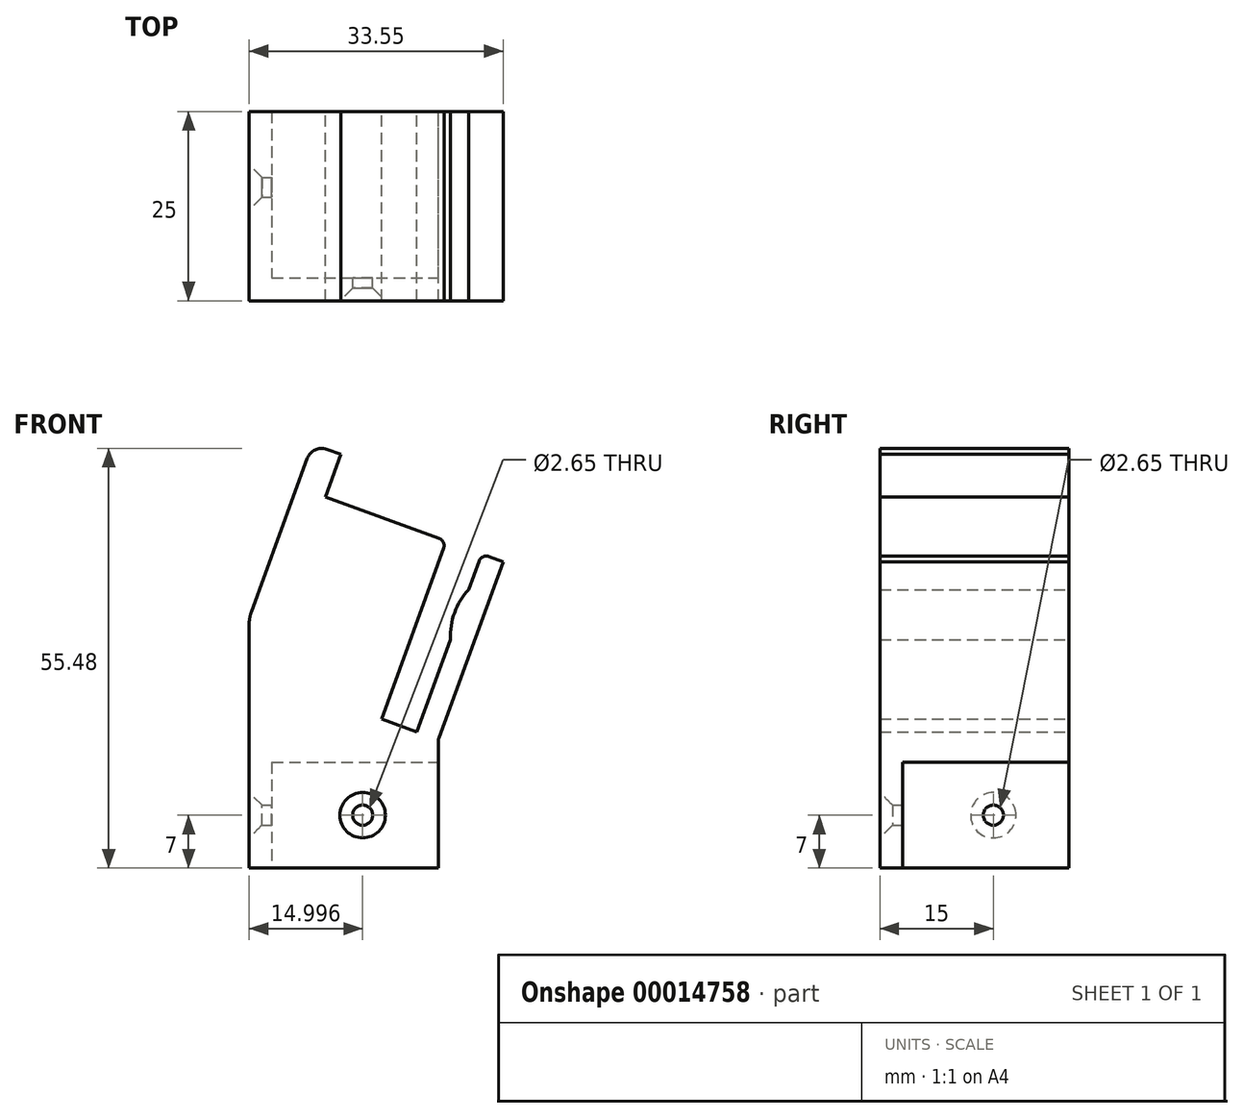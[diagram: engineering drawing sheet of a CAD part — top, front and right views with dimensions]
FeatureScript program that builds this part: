
annotation { "Feature Type Name" : "Feature", "Feature Type Description" : "" }
export const myFeature = defineFeature(function(context is Context, id is Id, definition is map)
    precondition{}
    {
        {
            var Q0;
            Q0=qCreatedBy(makeId("Front.planeOp"),FACE);
            var sketch = newSketch(context, id + "F0", { "sketchPlane" : qUnion([Q0])});
            skLineSegment(sketch, "E0", {"start": v(-18.57, 0) * mm, "end": v(-18.57, 18.15) * mm});
            skLineSegment(sketch, "E1", {"start": v(-8.32, 41.36) * mm, "end": v(-6.46, 40.68) * mm});
            skLineSegment(sketch, "E2", {"start": v(-6.46, 40.68) * mm, "end": v(-8.52, 35.04) * mm});
            skLineSegment(sketch, "E3", {"start": v(-8.52, 35.04) * mm, "end": v(6.52, 29.57) * mm});
            skLineSegment(sketch, "E4", {"start": v(7.12, 28.29) * mm, "end": v(-1.1, 5.74) * mm});
            skLineSegment(sketch, "E5", {"start": v(-1.1, 5.74) * mm, "end": v(3.6, 4.03) * mm});
            skLineSegment(sketch, "E6", {"start": v(3.6, 4.03) * mm, "end": v(8.04, 16.2) * mm});
            skArc(sketch, "E7", {"start": v(10.45, 22.82) * mm, "mid": v(8.56, 19.76) * mm, "end": v(8.04, 16.2) * mm});
            skLineSegment(sketch, "E8", {"start": v(10.45, 22.82) * mm, "end": v(11.82, 26.58) * mm});
            skLineSegment(sketch, "E9", {"start": v(13.1, 27.18) * mm, "end": v(14.98, 26.5) * mm});
            skLineSegment(sketch, "E10", {"start": v(14.98, 26.5) * mm, "end": v(6.49, 3.17) * mm});
            skLineSegment(sketch, "E11", {"start": v(6.43, 2.82) * mm, "end": v(6.43, 0) * mm});
            skLineSegment(sketch, "E12", {"start": v(6.43, 0) * mm, "end": v(-18.57, 0) * mm});
            skLineSegment(sketch, "E13", {"start": v(7.46, 29.23) * mm, "end": v(11.02, 27.93) * mm, "construction": true});
            skLineSegment(sketch, "E14", {"start": v(3.6, 4.03) * mm, "end": v(9.61, 1.84) * mm, "construction": true});
            skLineSegment(sketch, "E15", {"start": v(-10.88, 40.16) * mm, "end": v(-18.27, 19.86) * mm});
            skPoint(sketch, "E15.endSnap0", {"position": v(-18.57, 19.9) * mm});
            skPoint(sketch, "E16.orphan", {"position": v(-18.57, 39.81) * mm});
            skLineSegment(sketch, "E17", {"start": v(-18.57, 0) * mm, "end": v(-18.57, -14) * mm});
            skLineSegment(sketch, "E18", {"start": v(-18.57, -14) * mm, "end": v(6.43, -14) * mm});
            skLineSegment(sketch, "E19", {"start": v(6.43, -14) * mm, "end": v(6.43, 0) * mm});
            skPoint(sketch, "E20.visualSharp", {"position": v(-18.57, 19.04) * mm});
            skArc(sketch, "E20.filletArc", {"start": v(-18.27, 19.86) * mm, "mid": v(-18.5, 19.02) * mm, "end": v(-18.57, 18.15) * mm});
            skPoint(sketch, "E21.visualSharp", {"position": v(-10.2, 42.04) * mm});
            skArc(sketch, "E21.filletArc", {"start": v(-8.32, 41.36) * mm, "mid": v(-9.85, 41.3) * mm, "end": v(-10.88, 40.16) * mm});
            skPoint(sketch, "E22.visualSharp", {"position": v(12.16, 27.52) * mm});
            skArc(sketch, "E22.filletArc", {"start": v(13.1, 27.18) * mm, "mid": v(12.33, 27.14) * mm, "end": v(11.82, 26.58) * mm});
            skPoint(sketch, "E23.visualSharp", {"position": v(7.46, 29.23) * mm});
            skArc(sketch, "E23.filletArc", {"start": v(7.12, 28.29) * mm, "mid": v(7.08, 29.05) * mm, "end": v(6.52, 29.57) * mm});
            skPoint(sketch, "E24.visualSharp", {"position": v(6.43, 3) * mm});
            skArc(sketch, "E24.filletArc", {"start": v(6.49, 3.17) * mm, "mid": v(6.44, 3) * mm, "end": v(6.43, 2.82) * mm});
            skSolve(sketch);
        }
        {
            var Q0;
            Q0=makeQuery(id+"F0.imprint","IMPRINT",FACE,{"disambiguationData":[TD([[makeQuery(id+"F0.imprint","IMPRINT",EDGE,{"derivedFrom":sQuery(id+"F0.wireOp",EDGE,"E0")}),-1.0]])]});
            var Q1;
            Q1=makeQuery(id+"F0.imprint","IMPRINT",FACE,{"disambiguationData":[TD([[makeQuery(id+"F0.imprint","IMPRINT",EDGE,{"derivedFrom":sQuery(id+"F0.wireOp",EDGE,"E12")}),1.0]])]});
            extrude(context, id + "F1", {"entities" : qUnion([Q0, Q1]), "depth" : 25 * mm});
        }
        {
            var Q0;
            Q0=makeQuery(id+"F1.opExtrude","SWEPT_FACE",FACE,{"disambiguationData":[OSD([sQuery(id+"F0.wireOp",EDGE,"E18")])]});
            var sketch = newSketch(context, id + "F2", { "sketchPlane" : qUnion([Q0])});
            skLineSegment(sketch, "E25.bottom", {"start": v(-15.57, 0) * mm, "end": v(6.43, 0) * mm});
            skLineSegment(sketch, "E25.top", {"start": v(-15.57, 22) * mm, "end": v(6.43, 22) * mm});
            skLineSegment(sketch, "E25.left", {"start": v(-15.57, 0) * mm, "end": v(-15.57, 22) * mm});
            skLineSegment(sketch, "E25.right", {"start": v(6.43, 0) * mm, "end": v(6.43, 22) * mm});
            skSolve(sketch);
        }
        {
            var Q0;
            Q0=makeQuery(id+"F2.imprint","IMPRINT",FACE,{"disambiguationData":[TD([[makeQuery(id+"F2.imprint","IMPRINT",EDGE,{"derivedFrom":sQuery(id+"F2.wireOp",EDGE,"E25.bottom")}),1.0]])]});
            extrude(context, id + "F3", {"entities" : qUnion([Q0]), "operationType" : NewBodyOperationType.REMOVE, "oppositeDirection" : true, "depth" : 14 * mm});
        }
        {
            var Q0;
            Q0=makeQuery(id+"F1.opExtrude","CAP_FACE",FACE,{"disambiguationData":[OSD([sQuery(id+"F0.wireOp",EDGE,"E0"),sQuery(id+"F0.wireOp",EDGE,"E1"),sQuery(id+"F0.wireOp",EDGE,"E2"),sQuery(id+"F0.wireOp",EDGE,"E3"),sQuery(id+"F0.wireOp",EDGE,"E4"),sQuery(id+"F0.wireOp",EDGE,"E5"),sQuery(id+"F0.wireOp",EDGE,"E6"),sQuery(id+"F0.wireOp",EDGE,"E7"),sQuery(id+"F0.wireOp",EDGE,"E8"),sQuery(id+"F0.wireOp",EDGE,"E9"),sQuery(id+"F0.wireOp",EDGE,"E10"),sQuery(id+"F0.wireOp",EDGE,"E11"),sQuery(id+"F0.wireOp",EDGE,"E15"),sQuery(id+"F0.wireOp",EDGE,"E17"),sQuery(id+"F0.wireOp",EDGE,"E18"),sQuery(id+"F0.wireOp",EDGE,"E19"),sQuery(id+"F0.wireOp",EDGE,"E20.filletArc"),sQuery(id+"F0.wireOp",EDGE,"E21.filletArc"),sQuery(id+"F0.wireOp",EDGE,"E22.filletArc"),sQuery(id+"F0.wireOp",EDGE,"E23.filletArc"),sQuery(id+"F0.wireOp",EDGE,"E24.filletArc")])],"isStart":false});
            var sketch = newSketch(context, id + "F4", { "sketchPlane" : qUnion([Q0])});
            skPoint(sketch, "E26", {"position": v(-3.57, -7) * mm});
            skSolve(sketch);
        }
        {
            var Q0;
            Q0=makeQuery(id+"F1.opExtrude","SWEPT_FACE",FACE,{"disambiguationData":[OSD([sQuery(id+"F0.wireOp",EDGE,"E0"),sQuery(id+"F0.wireOp",EDGE,"E17")])]});
            var sketch = newSketch(context, id + "F5", { "sketchPlane" : qUnion([Q0])});
            skPoint(sketch, "E27", {"position": v(10, -7) * mm});
            skSolve(sketch);
        }
        {
            var Q0;
            Q0=sQuery(id+"F5.wireOp",VERTEX,"E27");
            var Q1;
            Q1=makeQuery(id+"F1.opExtrude","SWEPT_BODY",BODY,{"disambiguationData":[OSD([sQuery(id+"F0.wireOp",EDGE,"E0"),sQuery(id+"F0.wireOp",EDGE,"E1"),sQuery(id+"F0.wireOp",EDGE,"E2"),sQuery(id+"F0.wireOp",EDGE,"E3"),sQuery(id+"F0.wireOp",EDGE,"E4"),sQuery(id+"F0.wireOp",EDGE,"E5"),sQuery(id+"F0.wireOp",EDGE,"E6"),sQuery(id+"F0.wireOp",EDGE,"E7"),sQuery(id+"F0.wireOp",EDGE,"E8"),sQuery(id+"F0.wireOp",EDGE,"E9"),sQuery(id+"F0.wireOp",EDGE,"E10"),sQuery(id+"F0.wireOp",EDGE,"E11"),sQuery(id+"F0.wireOp",EDGE,"E15"),sQuery(id+"F0.wireOp",EDGE,"E17"),sQuery(id+"F0.wireOp",EDGE,"E18"),sQuery(id+"F0.wireOp",EDGE,"E19"),sQuery(id+"F0.wireOp",EDGE,"E20.filletArc"),sQuery(id+"F0.wireOp",EDGE,"E21.filletArc"),sQuery(id+"F0.wireOp",EDGE,"E22.filletArc"),sQuery(id+"F0.wireOp",EDGE,"E23.filletArc"),sQuery(id+"F0.wireOp",EDGE,"E24.filletArc")])]});
            hole(context, id + "F6", {"style" : HoleStyle.C_SINK, "endStyle" : HoleEndStyle.BLIND, "holeDiameter" : 2.65 * mm, "cSinkDiameter" : 6 * mm, "cSinkAngle" : 90 * degree, "holeDepth" : 6 * mm, "locations" : qUnion([Q0]), "scope" : qUnion([Q1]), "startStyle" : HoleStartStyle.SKETCH});
        }
        {
            var Q0;
            Q0=sQuery(id+"F4.wireOp",VERTEX,"E26");
            var Q1;
            Q1=makeQuery(id+"F1.opExtrude","SWEPT_BODY",BODY,{"disambiguationData":[OSD([sQuery(id+"F0.wireOp",EDGE,"E0"),sQuery(id+"F0.wireOp",EDGE,"E1"),sQuery(id+"F0.wireOp",EDGE,"E2"),sQuery(id+"F0.wireOp",EDGE,"E3"),sQuery(id+"F0.wireOp",EDGE,"E4"),sQuery(id+"F0.wireOp",EDGE,"E5"),sQuery(id+"F0.wireOp",EDGE,"E6"),sQuery(id+"F0.wireOp",EDGE,"E7"),sQuery(id+"F0.wireOp",EDGE,"E8"),sQuery(id+"F0.wireOp",EDGE,"E9"),sQuery(id+"F0.wireOp",EDGE,"E10"),sQuery(id+"F0.wireOp",EDGE,"E11"),sQuery(id+"F0.wireOp",EDGE,"E15"),sQuery(id+"F0.wireOp",EDGE,"E17"),sQuery(id+"F0.wireOp",EDGE,"E18"),sQuery(id+"F0.wireOp",EDGE,"E19"),sQuery(id+"F0.wireOp",EDGE,"E20.filletArc"),sQuery(id+"F0.wireOp",EDGE,"E21.filletArc"),sQuery(id+"F0.wireOp",EDGE,"E22.filletArc"),sQuery(id+"F0.wireOp",EDGE,"E23.filletArc"),sQuery(id+"F0.wireOp",EDGE,"E24.filletArc")])]});
            hole(context, id + "F7", {"style" : HoleStyle.C_SINK, "endStyle" : HoleEndStyle.BLIND, "holeDiameter" : 2.65 * mm, "cSinkDiameter" : 6 * mm, "cSinkAngle" : 90 * degree, "holeDepth" : 6 * mm, "locations" : qUnion([Q0]), "scope" : qUnion([Q1]), "startStyle" : HoleStartStyle.SKETCH});
        }
    });
